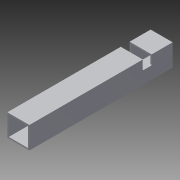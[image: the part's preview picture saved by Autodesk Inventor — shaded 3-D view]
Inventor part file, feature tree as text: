
AUTODESK INVENTOR PART (.ipt)
format: ipt  version: 2013 (Build 170138000, 138)  size: 92,672 bytes
history: native  units: in
note: dims shown in document units (in); Inventor stores cm internally (conversion verified against a paired STEP export)
features: extrude x2, sketch x2, reference x1
ambient origin geometry x8: Origin, YZ Plane, XZ Plane, XY Plane, X Axis, Y Axis, Z Axis, Center Point
bodies: Solid1 (feature_tree)
feature tree (5):
  extrude  "Extrusion1"  Depth=1.0in
  extrude  "Extrusion2"  Depth=6.5in TaperAngle=0.0deg
  sketch  "Sketch1"  dims[d0=1.0in d1=1.0in]
  sketch  "Sketch2"  dims[d2=0.0625in d3=6.5in d4=0.0in d5=1.0in d6=0.0in]
  reference  "Reference1"
